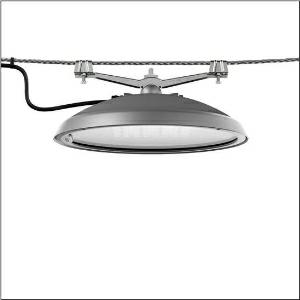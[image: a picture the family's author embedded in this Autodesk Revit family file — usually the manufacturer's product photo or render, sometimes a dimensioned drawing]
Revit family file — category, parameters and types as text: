
# Revit family: dl_r__50_iq_mini___st1_0s_5xa248w31f08re_8883
name_source: partatom
category: Lighting Fixtures
units: mm (PartAtom-declared; Revit-internal decimal feet)

## family parameters
Cut with Voids When Loaded = No
Host = Face
Light Source = No
Part Type = Normal
Room Calculation Point = No
Round Connector Dimension = Use Diameter
Shared = No

## types (1)
- --- (1 x LED, 6000 lm, 35.4 W, 3000K)
    Apparent Load = 35 VA
    CIE Flux Codes = 37 72 97 100 100
    Color Rendering = 70
    Color Temperature = 3000K
    Default Elevation = 1800 mm
    Description = DL® 50 iQ mini, catenary luminaire, primary light control with lens, of PMMA, primary optical cover: cover, of toughened safety glass, transparent, light distribution: ST1.0s, light emission: direct distribution, primary light characteristic: symmetric, installation type: suspended mounting, LED, High Power LED, rated luminous flux: 6.000lm, luminous efficacy: 170lm/W, light colour: 730, colour temperature: 3000K, control gear: iQ Street-Remote, control: optimised constant luminous flux control (CLO 2.0), Desk-Remote (wireless, voltage-free reading and setting of iQ features in the workshop via application-optimized NFC function/RFID function), Light-Fading, Smart-Wire, Night-Set, Lumen-Switch, Temp-Guard, Auto-Match, Street-Remote, mains connection: 230..240V, AC, 50/60Hz, start of lifetime: 35W, end of service life: 36W, reduction: 17W, luminaire housing, of diecast aluminium, powder-coated, Siteco® metallic grey (DB 702S), diameter: 500mm, height: 115mm, mounting height: 4..12m, protection rating (complete): IP66, insulation class (complete): insulation class II (safety insulation), certification: CE, ENEC, ENEC+, VDE, impact resistance: IK08, permissible operating ambient temperature for outdoor applications: -25..+40°C, standard-compliant lighting for roads and squares, packaging unit: 1 piece

Light Distribution: ST1.0s
    Height = 124 mm  [stored 0.406824 ft]
    Lamp = 1 x LED
    Lamp Light Flux = 6000 lm
    Lamp Power = 35.4 W
    Lamp count = 1
    Length = 500 mm
    Luminous efficacy = 169 lm/W
    Manufacturer = Siteco
    ModVariant = No
    Model = 5XA248W31F08RE
    Number of Poles = 1
    OnlyDefault = Yes
    Power Factor = 1
    Product Name = DL® 50 iQ mini | ST1.0s
    Product group = catenary luminaire
    ProductGroupID = 6300
    Protection Class = Protection class II
    Protection Degree = IP 66
    RLX_Detail_Level = 1
    RLX_Emergency_Light_Flux = 0 lm
    RLX_Emergency_Type = 0
    RLX_Emergency_Type_DB = No
    RlxData = <blob elided: 123709 chars, md5=ccab8412>
    Socket = socket
    Standby Power = 0 W
    System Light Flux = 6000 lm
    System Power = 35 W
    Type Comments = factory setting: luminous flux: 100 % | dim-lin: 254 | 376 mA
    Type Image = l_1242791.jpg
    URL = http://relux.com
    VarID = @adj_140754
    Voltage = 0 V
    Weight = 0.00 kg
    Width = 0 mm  [stored 0 ft]

note: [stored X ft] marks values corroborated as IEEE doubles in the binary element streams (Revit-internal decimal feet)

## geometry (parser evidence)
native form markers: Blend x4, Sweep x14
no freeform markers — native parametric forms only
